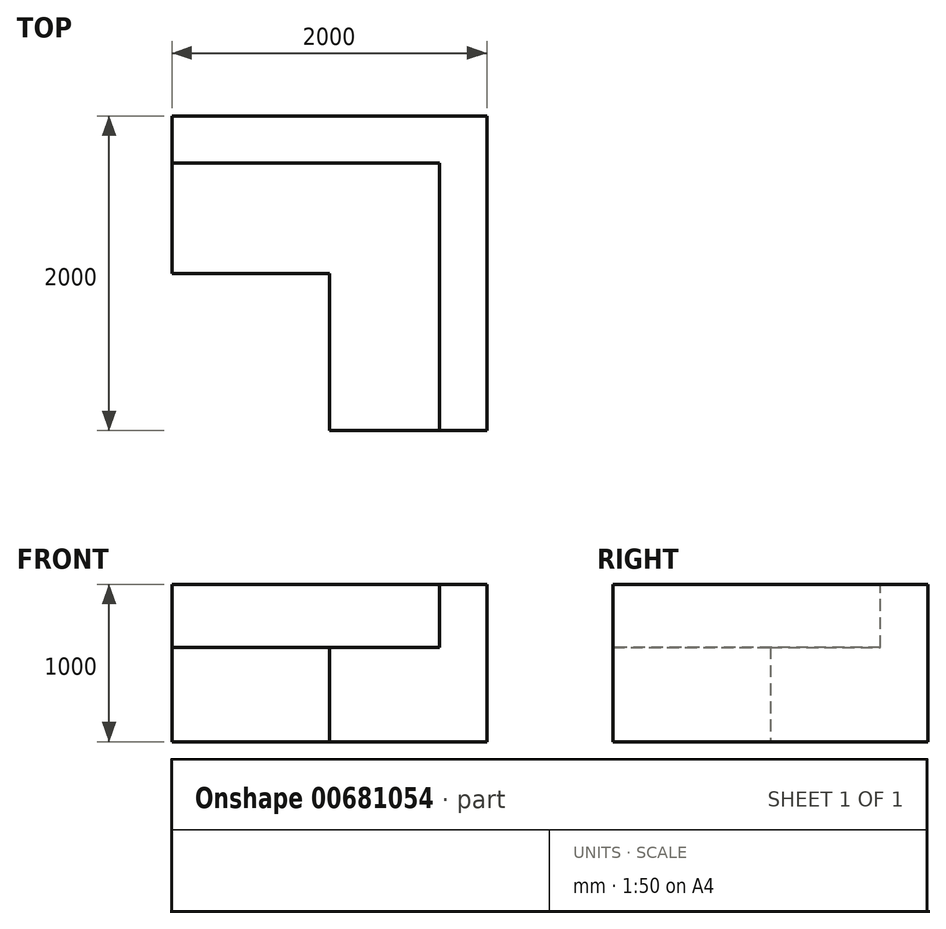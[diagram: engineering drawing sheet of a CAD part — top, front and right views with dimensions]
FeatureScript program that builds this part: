
annotation { "Feature Type Name" : "Feature", "Feature Type Description" : "" }
export const myFeature = defineFeature(function(context is Context, id is Id, definition is map)
    precondition{}
    {
        {
            var Q0;
            Q0=qCreatedBy(makeId("Top.planeOp"),FACE);
            var sketch = newSketch(context, id + "F0", { "sketchPlane" : qUnion([Q0])});
            skLineSegment(sketch, "E0", {"start": v(0, 0) * mm, "end": v(-1000, 0) * mm});
            skLineSegment(sketch, "E1", {"start": v(-1000, 0) * mm, "end": v(-1000, 1000) * mm});
            skLineSegment(sketch, "E2", {"start": v(-1000, 1000) * mm, "end": v(-2000, 1000) * mm});
            skLineSegment(sketch, "E3", {"start": v(-2000, 1000) * mm, "end": v(-2000, 2000) * mm});
            skLineSegment(sketch, "E4", {"start": v(-2000, 2000) * mm, "end": v(0, 2000) * mm});
            skLineSegment(sketch, "E5", {"start": v(0, 2000) * mm, "end": v(0, 0) * mm});
            skSolve(sketch);
        }
        {
            var Q0;
            Q0 = qSketchRegion(id + "F0", true);
            extrude(context, id + "F1", {"entities" : qUnion([Q0]), "depth" : 1000 * mm, "offsetDistance" : 25 * mm});
        }
        {
            var Q0;
            Q0=makeQuery(id+"F1.opExtrude","CAP_FACE",FACE,{"disambiguationData":[OSD([sQuery(id+"F0.wireOp",EDGE,"E0"),sQuery(id+"F0.wireOp",EDGE,"E1"),sQuery(id+"F0.wireOp",EDGE,"E2"),sQuery(id+"F0.wireOp",EDGE,"E3"),sQuery(id+"F0.wireOp",EDGE,"E4"),sQuery(id+"F0.wireOp",EDGE,"E5")])],"isStart":false});
            var sketch = newSketch(context, id + "F2", { "sketchPlane" : qUnion([Q0])});
            skLineSegment(sketch, "E6", {"start": v(-2000, 1000) * mm, "end": v(-2000, 1700) * mm});
            skLineSegment(sketch, "E7", {"start": v(-2000, 1700) * mm, "end": v(-300, 1700) * mm});
            skLineSegment(sketch, "E8", {"start": v(-300, 1700) * mm, "end": v(-300, 0) * mm});
            skLineSegment(sketch, "E9", {"start": v(-300, 0) * mm, "end": v(-1000, 0) * mm});
            skLineSegment(sketch, "E10", {"start": v(-1000, 0) * mm, "end": v(-1000, 1000) * mm});
            skLineSegment(sketch, "E11", {"start": v(-1000, 1000) * mm, "end": v(-2000, 1000) * mm});
            skLineSegment(sketch, "E12", {"start": v(-1000, 1000) * mm, "end": v(-300, 1700) * mm, "construction": true});
            skSolve(sketch);
        }
        {
            var Q0;
            Q0 = qSketchRegion(id + "F2", true);
            extrude(context, id + "F3", {"entities" : qUnion([Q0]), "operationType" : NewBodyOperationType.REMOVE, "oppositeDirection" : true, "depth" : 400 * mm, "offsetDistance" : 25 * mm});
        }
    });
